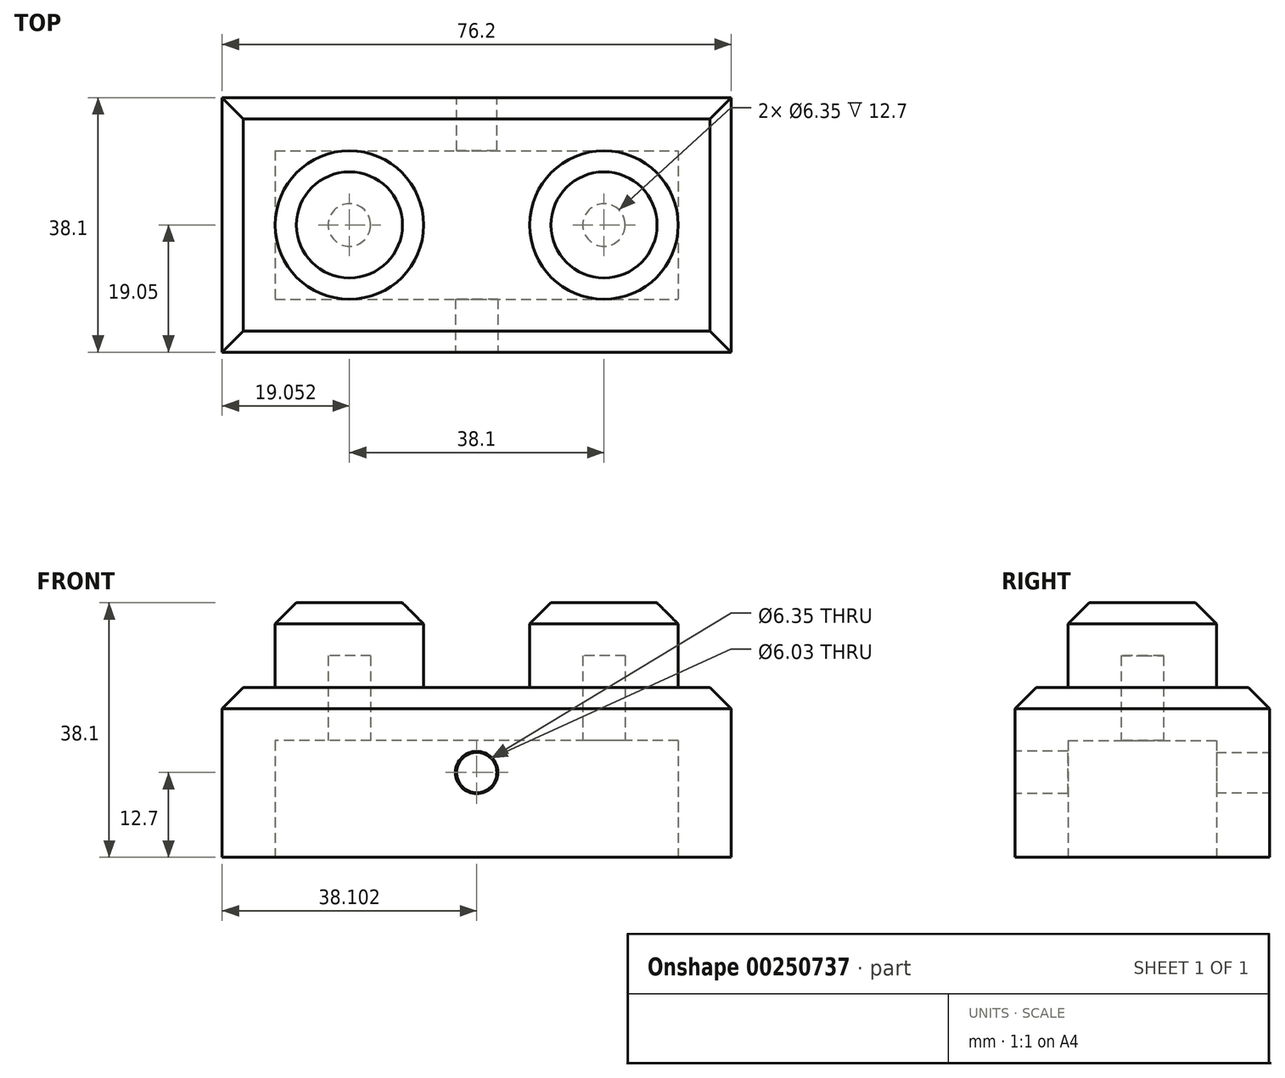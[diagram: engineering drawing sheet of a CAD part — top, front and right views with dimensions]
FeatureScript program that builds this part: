
annotation { "Feature Type Name" : "Feature", "Feature Type Description" : "" }
export const myFeature = defineFeature(function(context is Context, id is Id, definition is map)
    precondition{}
    {
        {
            var Q0;
            Q0=qCreatedBy(makeId("Top.planeOp"),FACE);
            var sketch = newSketch(context, id + "F0", { "sketchPlane" : qUnion([Q0])});
            skLineSegment(sketch, "E0.bottom", {"start": v(-43.98, 22.96) * mm, "end": v(32.22, 22.96) * mm});
            skLineSegment(sketch, "E0.top", {"start": v(-43.98, -15.14) * mm, "end": v(32.22, -15.14) * mm});
            skLineSegment(sketch, "E0.left", {"start": v(-43.98, 22.96) * mm, "end": v(-43.98, -15.14) * mm});
            skLineSegment(sketch, "E0.right", {"start": v(32.22, 22.96) * mm, "end": v(32.22, -15.14) * mm});
            skSolve(sketch);
        }
        {
            var Q0;
            Q0=makeQuery(id+"F0.imprint","IMPRINT",FACE,{"disambiguationData":[TD([[makeQuery(id+"F0.imprint","IMPRINT",EDGE,{"derivedFrom":sQuery(id+"F0.wireOp",EDGE,"E0.bottom")}),-1.0]])]});
            extrude(context, id + "F1", {"entities" : qUnion([Q0]), "depth" : 25.4 * mm});
        }
        {
            var Q0;
            Q0=makeQuery(id+"F1.opExtrude","CAP_FACE",FACE,{"disambiguationData":[OSD([sQuery(id+"F0.wireOp",EDGE,"E0.bottom"),sQuery(id+"F0.wireOp",EDGE,"E0.top"),sQuery(id+"F0.wireOp",EDGE,"E0.left"),sQuery(id+"F0.wireOp",EDGE,"E0.right")])],"isStart":false});
            var sketch = newSketch(context, id + "F2", { "sketchPlane" : qUnion([Q0])});
            skCircle(sketch, "E1", {"center": v(-24.93, 3.9) * mm, "radius": 11.11 * mm});
            skCircle(sketch, "E2", {"center": v(13.17, 3.9) * mm, "radius": 11.11 * mm});
            skPoint(sketch, "E3", {"position": v(-43.98, 3.9) * mm});
            skPoint(sketch, "E4", {"position": v(32.22, 3.9) * mm});
            skSolve(sketch);
        }
        {
            var Q0;
            Q0 = qSketchRegion(id + "F2", true);
            extrude(context, id + "F3", {"entities" : qUnion([Q0]), "operationType" : NewBodyOperationType.ADD, "depth" : 12.7 * mm});
        }
        {
            var Q0;
            Q0=makeQuery(id+"F3.opExtrude","CAP_EDGE",EDGE,{"disambiguationData":[OSD([sQuery(id+"F2.wireOp",EDGE,"E1")])],"isStart":false});
            var Q1;
            Q1=makeQuery(id+"F3.opExtrude","CAP_EDGE",EDGE,{"disambiguationData":[OSD([sQuery(id+"F2.wireOp",EDGE,"E2")])],"isStart":false});
            var Q2;
            Q2=makeQuery(id+"F1.opExtrude","CAP_EDGE",EDGE,{"disambiguationData":[OSD([sQuery(id+"F0.wireOp",EDGE,"E0.right")])],"isStart":false});
            var Q3;
            Q3=makeQuery(id+"F1.opExtrude","CAP_EDGE",EDGE,{"disambiguationData":[OSD([sQuery(id+"F0.wireOp",EDGE,"E0.bottom")])],"isStart":false});
            var Q4;
            Q4=makeQuery(id+"F1.opExtrude","CAP_EDGE",EDGE,{"disambiguationData":[OSD([sQuery(id+"F0.wireOp",EDGE,"E0.left")])],"isStart":false});
            var Q5;
            Q5=makeQuery(id+"F1.opExtrude","CAP_EDGE",EDGE,{"disambiguationData":[OSD([sQuery(id+"F0.wireOp",EDGE,"E0.top")])],"isStart":false});
            chamfer(context, id + "F4", {"entities" : qUnion([Q0, Q1, Q2, Q3, Q4, Q5]), "width" : 3.17 * mm, "tangentPropagation" : true});
        }
        {
            var Q0;
            Q0=makeQuery(id+"F1.opExtrude","CAP_FACE",FACE,{"disambiguationData":[OSD([sQuery(id+"F0.wireOp",EDGE,"E0.bottom"),sQuery(id+"F0.wireOp",EDGE,"E0.top"),sQuery(id+"F0.wireOp",EDGE,"E0.left"),sQuery(id+"F0.wireOp",EDGE,"E0.right")])],"isStart":true});
            shell(context, id + "F5", {"entities" : qUnion([Q0]), "thickness" : 7.94 * mm});
        }
        {
            var Q0;
            Q0=makeQuery(id+"F1.opExtrude","SWEPT_FACE",FACE,{"disambiguationData":[OSD([sQuery(id+"F0.wireOp",EDGE,"E0.top")])]});
            var sketch = newSketch(context, id + "F6", { "sketchPlane" : qUnion([Q0])});
            skCircle(sketch, "E5", {"center": v(-5.88, 12.7) * mm, "radius": 3.18 * mm});
            skSolve(sketch);
        }
        {
            var Q0;
            Q0=makeQuery(id+"F6.imprint","IMPRINT",FACE,{"disambiguationData":[TD([[makeQuery(id+"F6.imprint","IMPRINT",EDGE,{"derivedFrom":sQuery(id+"F6.wireOp",EDGE,"E5")}),1.0]])]});
            extrude(context, id + "F7", {"entities" : qUnion([Q0]), "operationType" : NewBodyOperationType.REMOVE, "oppositeDirection" : true, "depth" : 7.94 * mm});
        }
        {
            var Q0;
            Q0=makeQuery(id+"F1.opExtrude","SWEPT_FACE",FACE,{"disambiguationData":[OSD([sQuery(id+"F0.wireOp",EDGE,"E0.bottom")])]});
            var sketch = newSketch(context, id + "F8", { "sketchPlane" : qUnion([Q0])});
            skCircle(sketch, "E6", {"center": v(5.88, 12.7) * mm, "radius": 3.01 * mm});
            skSolve(sketch);
        }
        {
            var Q0;
            Q0=makeQuery(id+"F8.imprint","IMPRINT",FACE,{"disambiguationData":[TD([[makeQuery(id+"F8.imprint","IMPRINT",EDGE,{"derivedFrom":sQuery(id+"F8.wireOp",EDGE,"E6")}),1.0]])]});
            extrude(context, id + "F9", {"entities" : qUnion([Q0]), "operationType" : NewBodyOperationType.REMOVE, "oppositeDirection" : true, "depth" : 7.94 * mm});
        }
    });
